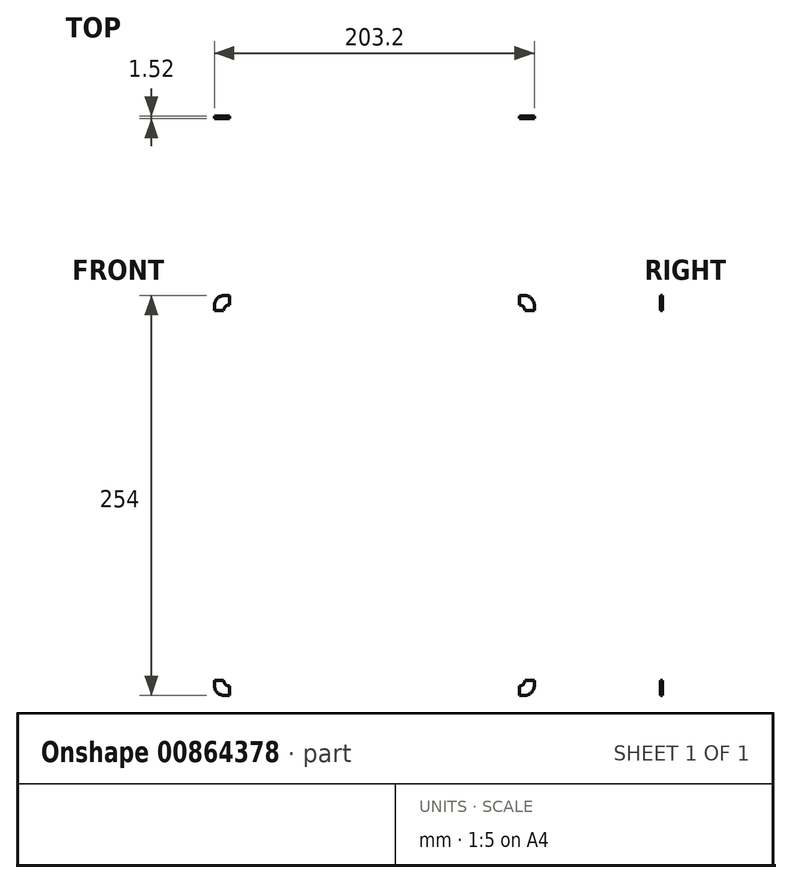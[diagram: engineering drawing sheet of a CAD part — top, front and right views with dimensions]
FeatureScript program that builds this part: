
annotation { "Feature Type Name" : "Feature", "Feature Type Description" : "" }
export const myFeature = defineFeature(function(context is Context, id is Id, definition is map)
    precondition{}
    {
        {
            var Q0;
            Q0=qCreatedBy(makeId("Front.planeOp"),FACE);
            var sketch = newSketch(context, id + "F0", { "sketchPlane" : qUnion([Q0])});
            skLineSegment(sketch, "E0.bottom", {"start": v(-100.35, 212.04) * mm, "end": v(90.15, 212.04) * mm});
            skLineSegment(sketch, "E0.top", {"start": v(-100.35, -41.96) * mm, "end": v(90.15, -41.96) * mm});
            skLineSegment(sketch, "E0.left", {"start": v(-106.7, 205.69) * mm, "end": v(-106.7, -35.61) * mm});
            skLineSegment(sketch, "E0.right", {"start": v(96.5, 205.69) * mm, "end": v(96.5, -35.61) * mm});
            skPoint(sketch, "E1.visualSharp", {"position": v(-106.7, 212.04) * mm});
            skArc(sketch, "E1.filletArc", {"start": v(-100.35, 212.04) * mm, "mid": v(-104.84, 210.18) * mm, "end": v(-106.7, 205.69) * mm});
            skPoint(sketch, "E2.visualSharp", {"position": v(96.5, 212.04) * mm});
            skArc(sketch, "E2.filletArc", {"start": v(96.5, 205.69) * mm, "mid": v(94.64, 210.18) * mm, "end": v(90.15, 212.04) * mm});
            skPoint(sketch, "E3.visualSharp", {"position": v(-106.7, -41.96) * mm});
            skArc(sketch, "E3.filletArc", {"start": v(-106.7, -35.61) * mm, "mid": v(-104.84, -40.1) * mm, "end": v(-100.35, -41.96) * mm});
            skPoint(sketch, "E4.visualSharp", {"position": v(96.5, -41.96) * mm});
            skArc(sketch, "E4.filletArc", {"start": v(90.15, -41.96) * mm, "mid": v(94.64, -40.1) * mm, "end": v(96.5, -35.61) * mm});
            skLineSegment(sketch, "E5.bottom", {"start": v(-106.7, 212.04) * mm, "end": v(-97.17, 212.04) * mm});
            skLineSegment(sketch, "E5.top", {"start": v(-106.7, 202.51) * mm, "end": v(-97.17, 202.51) * mm});
            skLineSegment(sketch, "E5.left", {"start": v(-106.7, 212.04) * mm, "end": v(-106.7, 202.51) * mm});
            skLineSegment(sketch, "E5.right", {"start": v(-97.17, 212.04) * mm, "end": v(-97.17, 202.51) * mm});
            skCircle(sketch, "E6", {"center": v(-97.17, 202.51) * mm, "radius": 3.57 * mm});
            skLineSegment(sketch, "E7.bottom", {"start": v(96.5, 212.04) * mm, "end": v(86.98, 212.04) * mm});
            skLineSegment(sketch, "E7.top", {"start": v(96.5, 202.51) * mm, "end": v(86.98, 202.51) * mm});
            skLineSegment(sketch, "E7.left", {"start": v(96.5, 212.04) * mm, "end": v(96.5, 202.51) * mm});
            skLineSegment(sketch, "E7.right", {"start": v(86.98, 212.04) * mm, "end": v(86.98, 202.51) * mm});
            skCircle(sketch, "E8", {"center": v(86.98, 202.51) * mm, "radius": 3.57 * mm});
            skLineSegment(sketch, "E9.bottom", {"start": v(-106.7, -41.96) * mm, "end": v(-97.17, -41.96) * mm});
            skLineSegment(sketch, "E9.top", {"start": v(-106.7, -32.44) * mm, "end": v(-97.17, -32.44) * mm});
            skLineSegment(sketch, "E9.left", {"start": v(-106.7, -41.96) * mm, "end": v(-106.7, -32.44) * mm});
            skLineSegment(sketch, "E9.right", {"start": v(-97.17, -41.96) * mm, "end": v(-97.17, -32.44) * mm});
            skLineSegment(sketch, "E10.bottom", {"start": v(96.5, -41.96) * mm, "end": v(86.98, -41.96) * mm});
            skLineSegment(sketch, "E10.top", {"start": v(96.5, -32.44) * mm, "end": v(86.98, -32.44) * mm});
            skLineSegment(sketch, "E10.left", {"start": v(96.5, -41.96) * mm, "end": v(96.5, -32.44) * mm});
            skLineSegment(sketch, "E10.right", {"start": v(86.98, -41.96) * mm, "end": v(86.98, -32.44) * mm});
            skCircle(sketch, "E11", {"center": v(-97.17, -32.44) * mm, "radius": 3.57 * mm});
            skCircle(sketch, "E12", {"center": v(86.98, -32.44) * mm, "radius": 3.57 * mm});
            skSolve(sketch);
        }
        {
            var Q0;
            {var subQ3=sQuery(id+"F0.wireOp",EDGE,"E1.filletArc");Q0=makeQuery(id+"F0.imprint","IMPRINT",FACE,{"disambiguationData":[TD([[makeQuery(id+"F0.imprint","IMPRINT",EDGE,{"derivedFrom":subQ3}),1.0]])]});}
            var Q1;
            {var subQ12=sQuery(id+"F0.wireOp",EDGE,"E0.bottom");Q1=makeQuery(id+"F0.imprint","IMPRINT",FACE,{"disambiguationData":[TD([[makeQuery(id+"F0.imprint","IMPRINT",EDGE,{"derivedFrom":subQ12}),-1.0]])]});}
            var Q2;
            {var subQ3=sQuery(id+"F0.wireOp",EDGE,"E2.filletArc");Q2=makeQuery(id+"F0.imprint","IMPRINT",FACE,{"disambiguationData":[TD([[makeQuery(id+"F0.imprint","IMPRINT",EDGE,{"derivedFrom":subQ3}),1.0]])]});}
            var Q3;
            {var subQ3=sQuery(id+"F0.wireOp",EDGE,"E3.filletArc");Q3=makeQuery(id+"F0.imprint","IMPRINT",FACE,{"disambiguationData":[TD([[makeQuery(id+"F0.imprint","IMPRINT",EDGE,{"derivedFrom":subQ3}),1.0]])]});}
            var Q4;
            {var subQ3=sQuery(id+"F0.wireOp",EDGE,"E4.filletArc");Q4=makeQuery(id+"F0.imprint","IMPRINT",FACE,{"disambiguationData":[TD([[makeQuery(id+"F0.imprint","IMPRINT",EDGE,{"derivedFrom":subQ3}),1.0]])]});}
            extrude(context, id + "F1", {"entities" : qUnion([Q0, Q1, Q2, Q3, Q4]), "depth" : 1.52 * mm, "offsetDistance" : 25.4 * mm});
        }
    });
